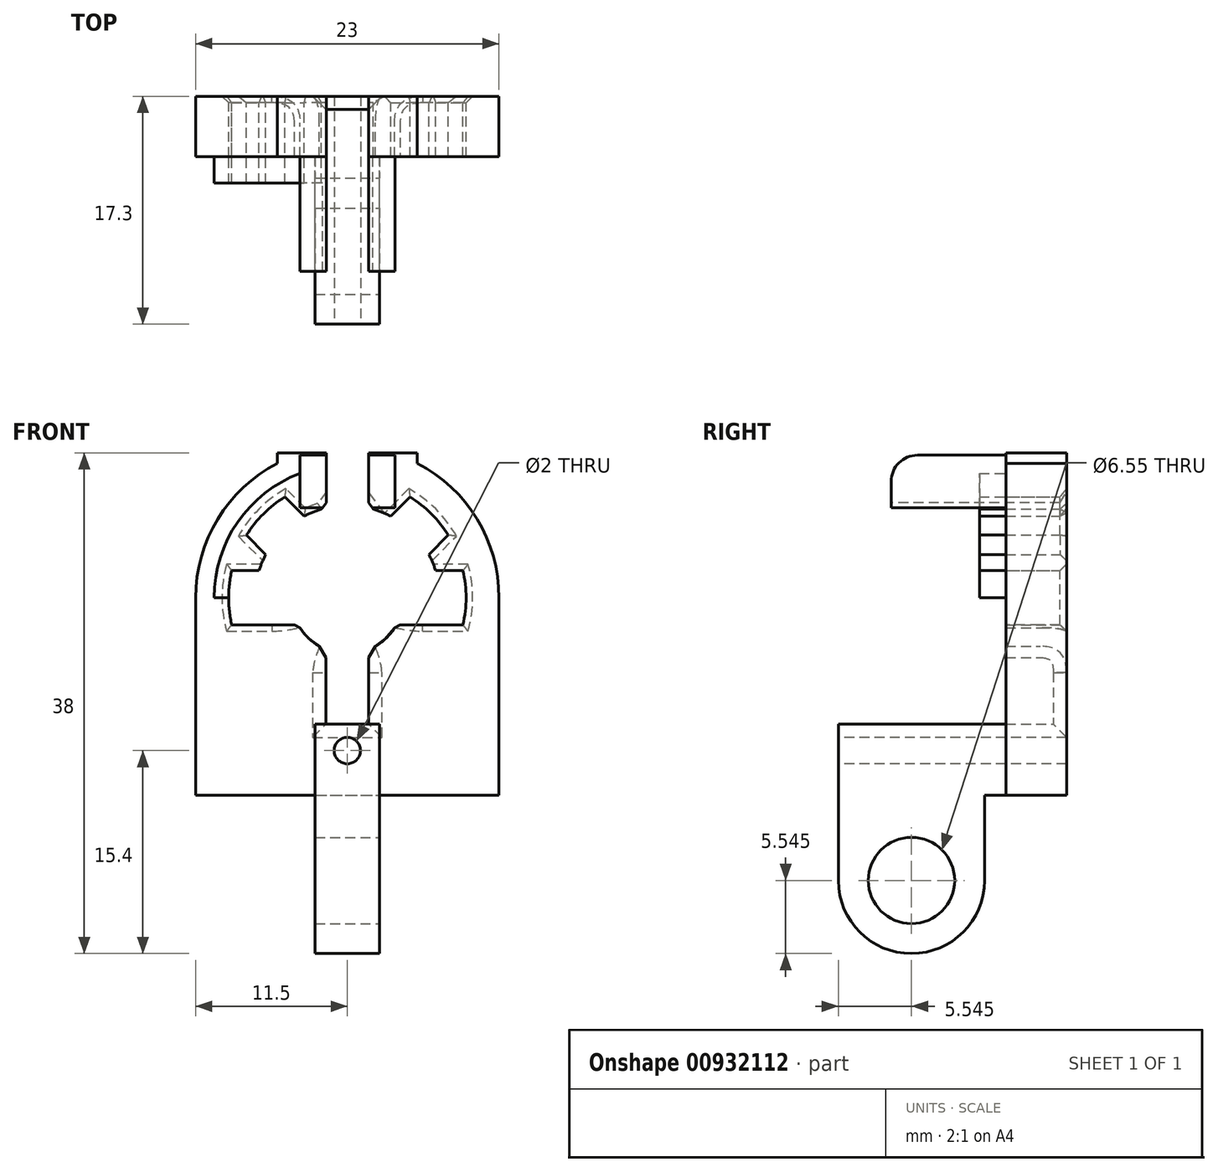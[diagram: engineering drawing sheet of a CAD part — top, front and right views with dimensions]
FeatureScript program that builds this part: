
annotation { "Feature Type Name" : "Feature", "Feature Type Description" : "" }
export const myFeature = defineFeature(function(context is Context, id is Id, definition is map)
    precondition{}
    {
        {
            var Q0;
            Q0=qCreatedBy(makeId("Front.planeOp"),FACE);
            var sketch = newSketch(context, id + "F0", { "sketchPlane" : qUnion([Q0])});
            skLineSegment(sketch, "E0", {"start": v(0, 0) * mm, "end": v(0, 30) * mm, "construction": true});
            skLineSegment(sketch, "E1.top", {"start": v(-11.5, 0) * mm, "end": v(11.5, 0) * mm});
            skPoint(sketch, "E1.middle", {"position": v(0, 15) * mm});
            skLineSegment(sketch, "E2", {"start": v(-11.5, 0) * mm, "end": v(-11.5, 15) * mm});
            skLineSegment(sketch, "E3", {"start": v(11.5, 0) * mm, "end": v(11.5, 15) * mm});
            skArc(sketch, "E4", {"start": v(11.5, 15) * mm, "mid": v(9.83, 20.97) * mm, "end": v(5.3, 25.2) * mm});
            skLineSegment(sketch, "E5.top", {"start": v(-5.3, 26) * mm, "end": v(-1.6, 26) * mm});
            skLineSegment(sketch, "E5.left", {"start": v(-5.3, 25.2) * mm, "end": v(-5.3, 26) * mm});
            skLineSegment(sketch, "E5.right", {"start": v(5.3, 25.2) * mm, "end": v(5.3, 26) * mm});
            skArc(sketch, "E6.trimOffspring", {"start": v(-5.3, 25.2) * mm, "mid": v(-9.83, 20.97) * mm, "end": v(-11.5, 15) * mm});
            skLineSegment(sketch, "E7.left", {"start": v(-1.6, 26) * mm, "end": v(-1.6, 21.81) * mm});
            skLineSegment(sketch, "E7.right", {"start": v(1.6, 26) * mm, "end": v(1.6, 21.81) * mm});
            skPoint(sketch, "E7.middle", {"position": v(0, 23.9) * mm});
            skArc(sketch, "E8", {"start": v(6.7, 17.05) * mm, "mid": v(6.47, 17.68) * mm, "end": v(6.18, 18.28) * mm});
            skLineSegment(sketch, "E9", {"start": v(8.76, 17.05) * mm, "end": v(6.7, 17.05) * mm});
            skLineSegment(sketch, "E10", {"start": v(8.76, 12.95) * mm, "end": v(6.7, 12.95) * mm});
            skLineSegment(sketch, "E11", {"start": v(1.6, 26) * mm, "end": v(5.3, 26) * mm});
            skLineSegment(sketch, "E12.1.0", {"start": v(4.75, 22.65) * mm, "end": v(3.28, 21.18) * mm});
            skLineSegment(sketch, "E12.1.1", {"start": v(7.65, 19.75) * mm, "end": v(6.18, 18.28) * mm});
            skLineSegment(sketch, "E12.3.0", {"start": v(-7.65, 19.75) * mm, "end": v(-6.18, 18.28) * mm});
            skLineSegment(sketch, "E12.3.1", {"start": v(-4.75, 22.65) * mm, "end": v(-3.28, 21.18) * mm});
            skLineSegment(sketch, "E12.4.0", {"start": v(-8.76, 12.95) * mm, "end": v(-6.7, 12.95) * mm});
            skLineSegment(sketch, "E12.4.1", {"start": v(-8.76, 17.05) * mm, "end": v(-6.7, 17.05) * mm});
            skArc(sketch, "E13.trimOffspring", {"start": v(-6.18, 18.28) * mm, "mid": v(-6.47, 17.68) * mm, "end": v(-6.7, 17.05) * mm});
            skArc(sketch, "E14.trimOffspring", {"start": v(-1.6, 21.81) * mm, "mid": v(-2.46, 21.55) * mm, "end": v(-3.28, 21.18) * mm});
            skArc(sketch, "E15.trimOffspring", {"start": v(3.28, 21.18) * mm, "mid": v(2.46, 21.55) * mm, "end": v(1.6, 21.81) * mm});
            skArc(sketch, "E16.trimOffspring", {"start": v(-8.76, 17.05) * mm, "mid": v(-9, 15) * mm, "end": v(-8.76, 12.95) * mm});
            skArc(sketch, "E17.trimOffspring", {"start": v(-4.75, 22.65) * mm, "mid": v(-6.36, 21.36) * mm, "end": v(-7.65, 19.75) * mm});
            skArc(sketch, "E18.trimOffspring", {"start": v(7.65, 19.75) * mm, "mid": v(6.36, 21.36) * mm, "end": v(4.75, 22.65) * mm});
            skArc(sketch, "E19.trimOffspring", {"start": v(8.76, 12.95) * mm, "mid": v(9, 15) * mm, "end": v(8.76, 17.05) * mm});
            skArc(sketch, "E20", {"start": v(-3.72, 12.95) * mm, "mid": v(-2.83, 11.83) * mm, "end": v(-1.62, 11.07) * mm});
            skLineSegment(sketch, "E21", {"start": v(-6.7, 12.95) * mm, "end": v(-3.72, 12.95) * mm});
            skLineSegment(sketch, "E22", {"start": v(6.7, 12.95) * mm, "end": v(3.72, 12.95) * mm});
            skLineSegment(sketch, "E23.top", {"start": v(-1.63, 5.4) * mm, "end": v(1.62, 5.4) * mm});
            skLineSegment(sketch, "E23.left", {"start": v(-1.63, 11.07) * mm, "end": v(-1.63, 5.4) * mm});
            skLineSegment(sketch, "E23.right", {"start": v(1.62, 11.07) * mm, "end": v(1.62, 5.4) * mm});
            skPoint(sketch, "E23.middle", {"position": v(0, 8.85) * mm});
            skArc(sketch, "E24.trimOffspring", {"start": v(1.62, 11.07) * mm, "mid": v(2.83, 11.83) * mm, "end": v(3.72, 12.95) * mm});
            skSolve(sketch);
        }
        {
            var Q0;
            Q0 = qSketchRegion(id + "F0", true);
            extrude(context, id + "F1", {"entities" : qUnion([Q0]), "depth" : 4.6 * mm, "offsetDistance" : 25 * mm});
        }
        {
            var Q0;
            Q0=makeQuery(id+"F1.opExtrude","CAP_FACE",FACE,{"disambiguationData":[OSD([sQuery(id+"F0.wireOp",EDGE,"E1.top"),sQuery(id+"F0.wireOp",EDGE,"E2"),sQuery(id+"F0.wireOp",EDGE,"E3"),sQuery(id+"F0.wireOp",EDGE,"E4"),sQuery(id+"F0.wireOp",EDGE,"E5.top"),sQuery(id+"F0.wireOp",EDGE,"E5.left"),sQuery(id+"F0.wireOp",EDGE,"E5.right"),sQuery(id+"F0.wireOp",EDGE,"E6.trimOffspring"),sQuery(id+"F0.wireOp",EDGE,"E7.left"),sQuery(id+"F0.wireOp",EDGE,"E7.right"),sQuery(id+"F0.wireOp",EDGE,"E8"),sQuery(id+"F0.wireOp",EDGE,"E9"),sQuery(id+"F0.wireOp",EDGE,"E10"),sQuery(id+"F0.wireOp",EDGE,"E11"),sQuery(id+"F0.wireOp",EDGE,"E12.1.0"),sQuery(id+"F0.wireOp",EDGE,"E12.1.1"),sQuery(id+"F0.wireOp",EDGE,"E12.3.0"),sQuery(id+"F0.wireOp",EDGE,"E12.3.1"),sQuery(id+"F0.wireOp",EDGE,"E12.4.0"),sQuery(id+"F0.wireOp",EDGE,"E12.4.1"),sQuery(id+"F0.wireOp",EDGE,"E13.trimOffspring"),sQuery(id+"F0.wireOp",EDGE,"E14.trimOffspring"),sQuery(id+"F0.wireOp",EDGE,"E15.trimOffspring"),sQuery(id+"F0.wireOp",EDGE,"E16.trimOffspring"),sQuery(id+"F0.wireOp",EDGE,"E17.trimOffspring"),sQuery(id+"F0.wireOp",EDGE,"E18.trimOffspring"),sQuery(id+"F0.wireOp",EDGE,"E19.trimOffspring"),sQuery(id+"F0.wireOp",EDGE,"E20"),sQuery(id+"F0.wireOp",EDGE,"E21"),sQuery(id+"F0.wireOp",EDGE,"E22"),sQuery(id+"F0.wireOp",EDGE,"E23.top"),sQuery(id+"F0.wireOp",EDGE,"E23.left"),sQuery(id+"F0.wireOp",EDGE,"E23.right"),sQuery(id+"F0.wireOp",EDGE,"E24.trimOffspring")])],"isStart":false});
            var sketch = newSketch(context, id + "F2", { "sketchPlane" : qUnion([Q0])});
            skLineSegment(sketch, "E25.bottom", {"start": v(-2.45, 5.4) * mm, "end": v(2.45, 5.4) * mm});
            skLineSegment(sketch, "E25.top", {"start": v(-2.45, -12) * mm, "end": v(2.45, -12) * mm});
            skLineSegment(sketch, "E25.left", {"start": v(-2.45, 5.4) * mm, "end": v(-2.45, -12) * mm});
            skLineSegment(sketch, "E25.right", {"start": v(2.45, 5.4) * mm, "end": v(2.45, -12) * mm});
            skPoint(sketch, "E25.middle", {"position": v(0, -3.3) * mm});
            skSolve(sketch);
        }
        {
            var Q0;
            Q0 = qSketchRegion(id + "F2", true);
            extrude(context, id + "F3", {"entities" : qUnion([Q0]), "operationType" : NewBodyOperationType.ADD, "depth" : 12.7 * mm, "offsetDistance" : 25 * mm});
        }
        {
            var Q0;
            Q0=makeQuery(id+"F3.opExtrude","SWEPT_FACE",FACE,{"disambiguationData":[OSD([sQuery(id+"F2.wireOp",EDGE,"E25.right")])]});
            var sketch = newSketch(context, id + "F4", { "sketchPlane" : qUnion([Q0])});
            skLineSegment(sketch, "E26.bottom", {"start": v(-4.6, 0) * mm, "end": v(-6.21, 0) * mm});
            skLineSegment(sketch, "E26.top", {"start": v(-4.6, -12) * mm, "end": v(-6.2, -12) * mm});
            skLineSegment(sketch, "E26.left", {"start": v(-4.6, 0) * mm, "end": v(-4.6, -12) * mm});
            skLineSegment(sketch, "E26.right", {"start": v(-6.21, 0) * mm, "end": v(-6.2, -12) * mm});
            skSolve(sketch);
        }
        {
            var Q0;
            Q0 = qSketchRegion(id + "F4", true);
            extrude(context, id + "F5", {"entities" : qUnion([Q0]), "operationType" : NewBodyOperationType.REMOVE, "oppositeDirection" : true, "depth" : 25 * mm, "offsetDistance" : 25 * mm});
        }
        {
            var Q0;
            Q0=makeQuery(id+"F3.opExtrude","SWEPT_FACE",FACE,{"disambiguationData":[OSD([sQuery(id+"F2.wireOp",EDGE,"E25.right")])]});
            var sketch = newSketch(context, id + "F6", { "sketchPlane" : qUnion([Q0])});
            skArc(sketch, "E27", {"start": v(-17.3, -6.45) * mm, "mid": v(-11.75, -12) * mm, "end": v(-6.2, -6.45) * mm});
            skPoint(sketch, "E27.centerSnap0", {"position": v(-11.75, -12) * mm});
            skLineSegment(sketch, "E28", {"start": v(-17.3, -6.45) * mm, "end": v(-17.3, -14.94) * mm});
            skLineSegment(sketch, "E29", {"start": v(-17.3, -14.94) * mm, "end": v(-6.2, -14.94) * mm});
            skLineSegment(sketch, "E30", {"start": v(-6.2, -14.94) * mm, "end": v(-6.2, -6.45) * mm});
            skCircle(sketch, "E31", {"center": v(-11.75, -6.45) * mm, "radius": 3.28 * mm});
            skSolve(sketch);
        }
        {
            var Q0;
            Q0 = qSketchRegion(id + "F6", true);
            extrude(context, id + "F7", {"entities" : qUnion([Q0]), "operationType" : NewBodyOperationType.REMOVE, "oppositeDirection" : true, "depth" : 25 * mm, "offsetDistance" : 25 * mm});
        }
        {
            var Q0;
            Q0=makeQuery(id+"F3.opExtrude","CAP_FACE",FACE,{"disambiguationData":[OSD([sQuery(id+"F2.wireOp",EDGE,"E25.bottom"),sQuery(id+"F2.wireOp",EDGE,"E25.top"),sQuery(id+"F2.wireOp",EDGE,"E25.left"),sQuery(id+"F2.wireOp",EDGE,"E25.right")])],"isStart":false});
            var sketch = newSketch(context, id + "F8", { "sketchPlane" : qUnion([Q0])});
            skCircle(sketch, "E32", {"center": v(0, 3.4) * mm, "radius": 1 * mm});
            skPoint(sketch, "E32.centerSnap0", {"position": v(0, 5.4) * mm});
            skSolve(sketch);
        }
        {
            var Q0;
            Q0 = qSketchRegion(id + "F8", true);
            extrude(context, id + "F9", {"entities" : qUnion([Q0]), "operationType" : NewBodyOperationType.REMOVE, "endBound" : BoundingType.THROUGH_ALL, "oppositeDirection" : true, "depth" : 25 * mm, "offsetDistance" : 25 * mm});
        }
        {
            var Q0;
            {var subQ0=sQuery(id+"F0.wireOp",EDGE,"E12.3.1");var subQ1=sQuery(id+"F0.wireOp",EDGE,"E24.trimOffspring");var subQ2=sQuery(id+"F0.wireOp",EDGE,"E23.right");var subQ3=sQuery(id+"F0.wireOp",EDGE,"E23.left");var subQ4=sQuery(id+"F0.wireOp",EDGE,"E23.top");var subQ5=sQuery(id+"F0.wireOp",EDGE,"E22");var subQ6=sQuery(id+"F0.wireOp",EDGE,"E21");var subQ7=sQuery(id+"F0.wireOp",EDGE,"E20");var subQ8=sQuery(id+"F0.wireOp",EDGE,"E19.trimOffspring");var subQ9=sQuery(id+"F0.wireOp",EDGE,"E18.trimOffspring");var subQ10=sQuery(id+"F0.wireOp",EDGE,"E17.trimOffspring");var subQ11=sQuery(id+"F0.wireOp",EDGE,"E16.trimOffspring");var subQ12=sQuery(id+"F0.wireOp",EDGE,"E15.trimOffspring");var subQ13=sQuery(id+"F0.wireOp",EDGE,"E14.trimOffspring");var subQ14=sQuery(id+"F0.wireOp",EDGE,"E13.trimOffspring");var subQ15=sQuery(id+"F0.wireOp",EDGE,"E12.4.1");var subQ16=sQuery(id+"F0.wireOp",EDGE,"E12.4.0");var subQ17=sQuery(id+"F0.wireOp",EDGE,"E12.3.0");var subQ18=sQuery(id+"F0.wireOp",EDGE,"E12.1.1");var subQ19=sQuery(id+"F0.wireOp",EDGE,"E12.1.0");var subQ20=sQuery(id+"F0.wireOp",EDGE,"E11");var subQ21=sQuery(id+"F0.wireOp",EDGE,"E10");var subQ22=sQuery(id+"F0.wireOp",EDGE,"E9");var subQ23=sQuery(id+"F0.wireOp",EDGE,"E8");var subQ24=sQuery(id+"F0.wireOp",EDGE,"E7.right");var subQ25=sQuery(id+"F0.wireOp",EDGE,"E7.left");var subQ26=sQuery(id+"F0.wireOp",EDGE,"E6.trimOffspring");var subQ27=sQuery(id+"F0.wireOp",EDGE,"E5.right");var subQ28=sQuery(id+"F0.wireOp",EDGE,"E5.left");var subQ29=sQuery(id+"F0.wireOp",EDGE,"E5.top");var subQ30=sQuery(id+"F0.wireOp",EDGE,"E4");var subQ31=sQuery(id+"F0.wireOp",EDGE,"E3");var subQ32=sQuery(id+"F0.wireOp",EDGE,"E2");var subQ33=sQuery(id+"F0.wireOp",EDGE,"E1.top");var subQ34=makeQuery(id+"F1.opExtrude","CAP_FACE",FACE,{"disambiguationData":[OSD([subQ33,subQ32,subQ31,subQ30,subQ29,subQ28,subQ27,subQ26,subQ25,subQ24,subQ23,subQ22,subQ21,subQ20,subQ19,subQ18,subQ17,subQ0,subQ16,subQ15,subQ14,subQ13,subQ12,subQ11,subQ10,subQ9,subQ8,subQ7,subQ6,subQ5,subQ4,subQ3,subQ2,subQ1])],"isStart":false});Q0=makeQuery(id+"F3.boolean.opBoolean","SPLIT",FACE,{"disambiguationData":[TD([makeQuery(id+"F1.opExtrude","SWEPT_FACE",FACE,{"disambiguationData":[OSD([subQ32])]})])],"derivedFrom":subQ34});}
            var sketch = newSketch(context, id + "F10", { "sketchPlane" : qUnion([Q0])});
            skLineSegment(sketch, "E33", {"start": v(-9, 15) * mm, "end": v(-10.1, 15) * mm});
            skArc(sketch, "E34", {"start": v(-1.6, 24.97) * mm, "mid": v(-7.69, 21.55) * mm, "end": v(-10.1, 15) * mm});
            skLineSegment(sketch, "E35", {"start": v(-1.6, 24.97) * mm, "end": v(-1.6, 21.81) * mm});
            skArc(sketch, "E36.0", {"start": v(-1.6, 21.81) * mm, "mid": v(-2.46, 21.55) * mm, "end": v(-3.28, 21.18) * mm});
            skArc(sketch, "E36.1", {"start": v(-6.18, 18.28) * mm, "mid": v(-6.47, 17.68) * mm, "end": v(-6.7, 17.05) * mm});
            skArc(sketch, "E36.2", {"start": v(-8.76, 17.05) * mm, "mid": v(-8.94, 16.03) * mm, "end": v(-9, 15) * mm});
            skLineSegment(sketch, "E37", {"start": v(-7.65, 19.75) * mm, "end": v(-6.18, 18.28) * mm});
            skArc(sketch, "E38.0", {"start": v(-4.75, 22.65) * mm, "mid": v(-6.36, 21.36) * mm, "end": v(-7.65, 19.75) * mm});
            skLineSegment(sketch, "E39", {"start": v(-4.75, 22.65) * mm, "end": v(-3.28, 21.18) * mm});
            skLineSegment(sketch, "E40", {"start": v(-8.76, 17.05) * mm, "end": v(-6.7, 17.05) * mm});
            skPoint(sketch, "E41.orphan", {"position": v(-8.76, 12.95) * mm});
            skSolve(sketch);
        }
        {
            var Q0;
            Q0=makeQuery(id+"F10.imprint","IMPRINT",FACE,{"disambiguationData":[TD([[makeQuery(id+"F10.imprint","IMPRINT",EDGE,{"derivedFrom":sQuery(id+"F10.wireOp",EDGE,"E33")}),-1.0]])]});
            extrude(context, id + "F11", {"entities" : qUnion([Q0]), "operationType" : NewBodyOperationType.ADD, "depth" : 2 * mm, "offsetDistance" : 25 * mm});
        }
        {
            var Q0;
            {var subQ0=sQuery(id+"F0.wireOp",EDGE,"E12.1.1");var subQ2=sQuery(id+"F0.wireOp",EDGE,"E22");var subQ3=sQuery(id+"F0.wireOp",EDGE,"E10");var subQ4=sQuery(id+"F0.wireOp",EDGE,"E9");var subQ5=sQuery(id+"F0.wireOp",EDGE,"E8");var subQ6=sQuery(id+"F0.wireOp",EDGE,"E7.right");var subQ8=sQuery(id+"F0.wireOp",EDGE,"E1.top");var subQ9=sQuery(id+"F0.wireOp",EDGE,"E12.1.0");var subQ10=sQuery(id+"F0.wireOp",EDGE,"E4");var subQ11=sQuery(id+"F0.wireOp",EDGE,"E19.trimOffspring");var subQ12=sQuery(id+"F0.wireOp",EDGE,"E3");var subQ13=sQuery(id+"F0.wireOp",EDGE,"E18.trimOffspring");var subQ14=sQuery(id+"F0.wireOp",EDGE,"E5.right");var subQ16=sQuery(id+"F0.wireOp",EDGE,"E15.trimOffspring");var subQ17=sQuery(id+"F0.wireOp",EDGE,"E23.top");var subQ18=sQuery(id+"F0.wireOp",EDGE,"E23.right");var subQ19=sQuery(id+"F0.wireOp",EDGE,"E24.trimOffspring");var subQ20=sQuery(id+"F0.wireOp",EDGE,"E23.left");var subQ21=sQuery(id+"F0.wireOp",EDGE,"E21");var subQ22=sQuery(id+"F0.wireOp",EDGE,"E20");var subQ23=sQuery(id+"F0.wireOp",EDGE,"E17.trimOffspring");var subQ24=sQuery(id+"F0.wireOp",EDGE,"E16.trimOffspring");var subQ25=sQuery(id+"F0.wireOp",EDGE,"E14.trimOffspring");var subQ26=sQuery(id+"F0.wireOp",EDGE,"E13.trimOffspring");var subQ27=sQuery(id+"F0.wireOp",EDGE,"E12.4.1");var subQ28=sQuery(id+"F0.wireOp",EDGE,"E12.4.0");var subQ29=sQuery(id+"F0.wireOp",EDGE,"E12.3.1");var subQ30=sQuery(id+"F0.wireOp",EDGE,"E12.3.0");var subQ31=sQuery(id+"F0.wireOp",EDGE,"E11");var subQ32=sQuery(id+"F0.wireOp",EDGE,"E7.left");var subQ33=sQuery(id+"F0.wireOp",EDGE,"E6.trimOffspring");var subQ34=sQuery(id+"F0.wireOp",EDGE,"E5.left");var subQ35=sQuery(id+"F0.wireOp",EDGE,"E5.top");var subQ36=sQuery(id+"F0.wireOp",EDGE,"E2");var subQ37=makeQuery(id+"F1.opExtrude","CAP_FACE",FACE,{"disambiguationData":[OSD([subQ8,subQ36,subQ12,subQ10,subQ35,subQ34,subQ14,subQ33,subQ32,subQ6,subQ5,subQ4,subQ3,subQ31,subQ9,subQ0,subQ30,subQ29,subQ28,subQ27,subQ26,subQ25,subQ16,subQ24,subQ23,subQ13,subQ11,subQ22,subQ21,subQ2,subQ17,subQ20,subQ18,subQ19])],"isStart":false});Q0=makeQuery(id+"F3.boolean.opBoolean","SPLIT",FACE,{"disambiguationData":[TD([makeQuery(id+"F1.opExtrude","SWEPT_FACE",FACE,{"disambiguationData":[OSD([subQ12])]})])],"derivedFrom":subQ37});}
            var sketch = newSketch(context, id + "F12", { "sketchPlane" : qUnion([Q0])});
            skLineSegment(sketch, "E42", {"start": v(1.6, 25.81) * mm, "end": v(3.6, 25.81) * mm});
            skLineSegment(sketch, "E43", {"start": v(3.6, 25.81) * mm, "end": v(3.6, 21.81) * mm});
            skLineSegment(sketch, "E44", {"start": v(3.6, 21.81) * mm, "end": v(1.6, 21.81) * mm});
            skLineSegment(sketch, "E45", {"start": v(0, 15) * mm, "end": v(0, 29.93) * mm, "construction": true});
            skLineSegment(sketch, "E46", {"start": v(1.6, 25.81) * mm, "end": v(1.6, 21.81) * mm});
            skLineSegment(sketch, "E47.MirrorCS", {"start": v(-3.6, 21.81) * mm, "end": v(-1.6, 21.81) * mm});
            skLineSegment(sketch, "E48.MirrorCS", {"start": v(-1.6, 25.81) * mm, "end": v(-1.6, 21.81) * mm});
            skLineSegment(sketch, "E49.MirrorCS", {"start": v(-3.6, 25.81) * mm, "end": v(-3.6, 21.81) * mm});
            skLineSegment(sketch, "E50.MirrorCS", {"start": v(-1.6, 25.81) * mm, "end": v(-3.6, 25.81) * mm});
            skSolve(sketch);
        }
        {
            var Q0;
            Q0 = qSketchRegion(id + "F12", true);
            extrude(context, id + "F13", {"entities" : qUnion([Q0]), "operationType" : NewBodyOperationType.ADD, "depth" : 8.7 * mm, "offsetDistance" : 25 * mm});
        }
        {
            var Q0;
            Q0=makeQuery(id+"F13.opExtrude","CAP_EDGE",EDGE,{"disambiguationData":[OSD([sQuery(id+"F12.wireOp",EDGE,"E42")])],"isStart":false});
            var Q1;
            Q1=makeQuery(id+"F13.opExtrude","CAP_EDGE",EDGE,{"disambiguationData":[OSD([sQuery(id+"F12.wireOp",EDGE,"E50.MirrorCS")])],"isStart":false});
            fillet(context, id + "F14", {"entities" : qUnion([Q0, Q1]), "radius" : 2 * mm, "tangentPropagation" : true, "allowEdgeOverflow" : false});
        }
        {
            var Q0;
            Q0=makeQuery(id+"F1.opExtrude","CAP_EDGE",EDGE,{"disambiguationData":[OSD([sQuery(id+"F0.wireOp",EDGE,"E24.trimOffspring")])],"isStart":true});
            var Q1;
            Q1=makeQuery(id+"F1.opExtrude","CAP_EDGE",EDGE,{"disambiguationData":[OSD([sQuery(id+"F0.wireOp",EDGE,"E20")])],"isStart":true});
            fillet(context, id + "F15", {"entities" : qUnion([Q0, Q1]), "radius" : 2 * mm, "tangentPropagation" : true, "rho" : 0.5, "crossSection" : FilletCrossSection.CONIC, "allowEdgeOverflow" : false});
        }
        {
            var Q0;
            Q0=makeQuery(id+"F1.opExtrude","CAP_EDGE",EDGE,{"disambiguationData":[OSD([sQuery(id+"F0.wireOp",EDGE,"E23.right")])],"isStart":true});
            var Q1;
            Q1=makeQuery(id+"F1.opExtrude","CAP_EDGE",EDGE,{"disambiguationData":[OSD([sQuery(id+"F0.wireOp",EDGE,"E23.left")])],"isStart":true});
            var Q2;
            Q2=makeQuery(id+"F1.opExtrude","CAP_EDGE",EDGE,{"disambiguationData":[OSD([sQuery(id+"F0.wireOp",EDGE,"E23.top")])],"isStart":true});
            chamfer(context, id + "F16", {"entities" : qUnion([Q0, Q1, Q2]), "width" : 1 * mm, "tangentPropagation" : true});
        }
        {
            var Q0;
            Q0=makeQuery(id+"F11.boolean.opBoolean","MERGE",EDGE,{"derivedFrom":[makeQuery(id+"F1.opExtrude","SWEPT_EDGE",EDGE,{"disambiguationData":[OSD([sQuery(id+"F0.wireOp",EDGE,"E7.left"),sQuery(id+"F0.wireOp",EDGE,"E14.trimOffspring")])]}),makeQuery(id+"F11.opExtrude","SWEPT_EDGE",EDGE,{"disambiguationData":[OSD([sQuery(id+"F10.wireOp",EDGE,"E35"),sQuery(id+"F10.wireOp",EDGE,"E36.0")])]})]});
            var Q1;
            Q1=makeQuery(id+"F1.opExtrude","SWEPT_EDGE",EDGE,{"disambiguationData":[OSD([sQuery(id+"F0.wireOp",EDGE,"E7.right"),sQuery(id+"F0.wireOp",EDGE,"E15.trimOffspring")])]});
            chamfer(context, id + "F17", {"entities" : qUnion([Q0, Q1]), "width" : 0.5 * mm, "tangentPropagation" : true});
        }
        {
            var Q0;
            Q0=makeQuery(id+"F1.opExtrude","CAP_EDGE",EDGE,{"disambiguationData":[OSD([sQuery(id+"F0.wireOp",EDGE,"E19.trimOffspring")])],"isStart":true});
            var Q1;
            Q1=makeQuery(id+"F1.opExtrude","CAP_EDGE",EDGE,{"disambiguationData":[OSD([sQuery(id+"F0.wireOp",EDGE,"E9")])],"isStart":true});
            var Q2;
            Q2=makeQuery(id+"F1.opExtrude","CAP_EDGE",EDGE,{"disambiguationData":[OSD([sQuery(id+"F0.wireOp",EDGE,"E12.1.1")])],"isStart":true});
            var Q3;
            Q3=makeQuery(id+"F1.opExtrude","CAP_EDGE",EDGE,{"disambiguationData":[OSD([sQuery(id+"F0.wireOp",EDGE,"E18.trimOffspring")])],"isStart":true});
            var Q4;
            Q4=makeQuery(id+"F1.opExtrude","CAP_EDGE",EDGE,{"disambiguationData":[OSD([sQuery(id+"F0.wireOp",EDGE,"E12.1.0")])],"isStart":true});
            var Q5;
            {var subQ0=sQuery(id+"F0.wireOp",EDGE,"E15.trimOffspring");var subQ1=sQuery(id+"F0.wireOp",EDGE,"E7.right");Q5=makeQuery(id+"F17.opChamfer","BLEND_EDGE",EDGE,{"blendedFrom":[makeQuery(id+"F1.opExtrude","SWEPT_EDGE",EDGE,{"disambiguationData":[OSD([subQ1,subQ0])]}),makeQuery(id+"F1.opExtrude","CAP_FACE",FACE,{"disambiguationData":[OSD([sQuery(id+"F0.wireOp",EDGE,"E1.top"),sQuery(id+"F0.wireOp",EDGE,"E2"),sQuery(id+"F0.wireOp",EDGE,"E3"),sQuery(id+"F0.wireOp",EDGE,"E4"),sQuery(id+"F0.wireOp",EDGE,"E5.top"),sQuery(id+"F0.wireOp",EDGE,"E5.left"),sQuery(id+"F0.wireOp",EDGE,"E5.right"),sQuery(id+"F0.wireOp",EDGE,"E6.trimOffspring"),sQuery(id+"F0.wireOp",EDGE,"E7.left"),subQ1,sQuery(id+"F0.wireOp",EDGE,"E8"),sQuery(id+"F0.wireOp",EDGE,"E9"),sQuery(id+"F0.wireOp",EDGE,"E10"),sQuery(id+"F0.wireOp",EDGE,"E11"),sQuery(id+"F0.wireOp",EDGE,"E12.1.0"),sQuery(id+"F0.wireOp",EDGE,"E12.1.1"),sQuery(id+"F0.wireOp",EDGE,"E12.3.0"),sQuery(id+"F0.wireOp",EDGE,"E12.3.1"),sQuery(id+"F0.wireOp",EDGE,"E12.4.0"),sQuery(id+"F0.wireOp",EDGE,"E12.4.1"),sQuery(id+"F0.wireOp",EDGE,"E13.trimOffspring"),sQuery(id+"F0.wireOp",EDGE,"E14.trimOffspring"),subQ0,sQuery(id+"F0.wireOp",EDGE,"E16.trimOffspring"),sQuery(id+"F0.wireOp",EDGE,"E17.trimOffspring"),sQuery(id+"F0.wireOp",EDGE,"E18.trimOffspring"),sQuery(id+"F0.wireOp",EDGE,"E19.trimOffspring"),sQuery(id+"F0.wireOp",EDGE,"E20"),sQuery(id+"F0.wireOp",EDGE,"E21"),sQuery(id+"F0.wireOp",EDGE,"E22"),sQuery(id+"F0.wireOp",EDGE,"E23.top"),sQuery(id+"F0.wireOp",EDGE,"E23.left"),sQuery(id+"F0.wireOp",EDGE,"E23.right"),sQuery(id+"F0.wireOp",EDGE,"E24.trimOffspring")])],"isStart":true})],"blendedInto":[makeQuery(id+"F1.opExtrude","CAP_FACE",FACE,{"disambiguationData":[OSD([sQuery(id+"F0.wireOp",EDGE,"E1.top"),sQuery(id+"F0.wireOp",EDGE,"E2"),sQuery(id+"F0.wireOp",EDGE,"E3"),sQuery(id+"F0.wireOp",EDGE,"E4"),sQuery(id+"F0.wireOp",EDGE,"E5.top"),sQuery(id+"F0.wireOp",EDGE,"E5.left"),sQuery(id+"F0.wireOp",EDGE,"E5.right"),sQuery(id+"F0.wireOp",EDGE,"E6.trimOffspring"),sQuery(id+"F0.wireOp",EDGE,"E7.left"),subQ1,sQuery(id+"F0.wireOp",EDGE,"E8"),sQuery(id+"F0.wireOp",EDGE,"E9"),sQuery(id+"F0.wireOp",EDGE,"E10"),sQuery(id+"F0.wireOp",EDGE,"E11"),sQuery(id+"F0.wireOp",EDGE,"E12.1.0"),sQuery(id+"F0.wireOp",EDGE,"E12.1.1"),sQuery(id+"F0.wireOp",EDGE,"E12.3.0"),sQuery(id+"F0.wireOp",EDGE,"E12.3.1"),sQuery(id+"F0.wireOp",EDGE,"E12.4.0"),sQuery(id+"F0.wireOp",EDGE,"E12.4.1"),sQuery(id+"F0.wireOp",EDGE,"E13.trimOffspring"),sQuery(id+"F0.wireOp",EDGE,"E14.trimOffspring"),subQ0,sQuery(id+"F0.wireOp",EDGE,"E16.trimOffspring"),sQuery(id+"F0.wireOp",EDGE,"E17.trimOffspring"),sQuery(id+"F0.wireOp",EDGE,"E18.trimOffspring"),sQuery(id+"F0.wireOp",EDGE,"E19.trimOffspring"),sQuery(id+"F0.wireOp",EDGE,"E20"),sQuery(id+"F0.wireOp",EDGE,"E21"),sQuery(id+"F0.wireOp",EDGE,"E22"),sQuery(id+"F0.wireOp",EDGE,"E23.top"),sQuery(id+"F0.wireOp",EDGE,"E23.left"),sQuery(id+"F0.wireOp",EDGE,"E23.right"),sQuery(id+"F0.wireOp",EDGE,"E24.trimOffspring")])],"isStart":true})]});}
            var Q6;
            {var subQ0=sQuery(id+"F0.wireOp",EDGE,"E14.trimOffspring");var subQ1=sQuery(id+"F0.wireOp",EDGE,"E7.left");Q6=makeQuery(id+"F17.opChamfer","BLEND_EDGE",EDGE,{"blendedFrom":[makeQuery(id+"F11.boolean.opBoolean","MERGE",EDGE,{"derivedFrom":[makeQuery(id+"F1.opExtrude","SWEPT_EDGE",EDGE,{"disambiguationData":[OSD([subQ1,subQ0])]}),makeQuery(id+"F11.opExtrude","SWEPT_EDGE",EDGE,{"disambiguationData":[OSD([sQuery(id+"F10.wireOp",EDGE,"E35"),sQuery(id+"F10.wireOp",EDGE,"E36.0")])]})]}),makeQuery(id+"F1.opExtrude","CAP_FACE",FACE,{"disambiguationData":[OSD([sQuery(id+"F0.wireOp",EDGE,"E1.top"),sQuery(id+"F0.wireOp",EDGE,"E2"),sQuery(id+"F0.wireOp",EDGE,"E3"),sQuery(id+"F0.wireOp",EDGE,"E4"),sQuery(id+"F0.wireOp",EDGE,"E5.top"),sQuery(id+"F0.wireOp",EDGE,"E5.left"),sQuery(id+"F0.wireOp",EDGE,"E5.right"),sQuery(id+"F0.wireOp",EDGE,"E6.trimOffspring"),subQ1,sQuery(id+"F0.wireOp",EDGE,"E7.right"),sQuery(id+"F0.wireOp",EDGE,"E8"),sQuery(id+"F0.wireOp",EDGE,"E9"),sQuery(id+"F0.wireOp",EDGE,"E10"),sQuery(id+"F0.wireOp",EDGE,"E11"),sQuery(id+"F0.wireOp",EDGE,"E12.1.0"),sQuery(id+"F0.wireOp",EDGE,"E12.1.1"),sQuery(id+"F0.wireOp",EDGE,"E12.3.0"),sQuery(id+"F0.wireOp",EDGE,"E12.3.1"),sQuery(id+"F0.wireOp",EDGE,"E12.4.0"),sQuery(id+"F0.wireOp",EDGE,"E12.4.1"),sQuery(id+"F0.wireOp",EDGE,"E13.trimOffspring"),subQ0,sQuery(id+"F0.wireOp",EDGE,"E15.trimOffspring"),sQuery(id+"F0.wireOp",EDGE,"E16.trimOffspring"),sQuery(id+"F0.wireOp",EDGE,"E17.trimOffspring"),sQuery(id+"F0.wireOp",EDGE,"E18.trimOffspring"),sQuery(id+"F0.wireOp",EDGE,"E19.trimOffspring"),sQuery(id+"F0.wireOp",EDGE,"E20"),sQuery(id+"F0.wireOp",EDGE,"E21"),sQuery(id+"F0.wireOp",EDGE,"E22"),sQuery(id+"F0.wireOp",EDGE,"E23.top"),sQuery(id+"F0.wireOp",EDGE,"E23.left"),sQuery(id+"F0.wireOp",EDGE,"E23.right"),sQuery(id+"F0.wireOp",EDGE,"E24.trimOffspring")])],"isStart":true})],"blendedInto":[makeQuery(id+"F1.opExtrude","CAP_FACE",FACE,{"disambiguationData":[OSD([sQuery(id+"F0.wireOp",EDGE,"E1.top"),sQuery(id+"F0.wireOp",EDGE,"E2"),sQuery(id+"F0.wireOp",EDGE,"E3"),sQuery(id+"F0.wireOp",EDGE,"E4"),sQuery(id+"F0.wireOp",EDGE,"E5.top"),sQuery(id+"F0.wireOp",EDGE,"E5.left"),sQuery(id+"F0.wireOp",EDGE,"E5.right"),sQuery(id+"F0.wireOp",EDGE,"E6.trimOffspring"),subQ1,sQuery(id+"F0.wireOp",EDGE,"E7.right"),sQuery(id+"F0.wireOp",EDGE,"E8"),sQuery(id+"F0.wireOp",EDGE,"E9"),sQuery(id+"F0.wireOp",EDGE,"E10"),sQuery(id+"F0.wireOp",EDGE,"E11"),sQuery(id+"F0.wireOp",EDGE,"E12.1.0"),sQuery(id+"F0.wireOp",EDGE,"E12.1.1"),sQuery(id+"F0.wireOp",EDGE,"E12.3.0"),sQuery(id+"F0.wireOp",EDGE,"E12.3.1"),sQuery(id+"F0.wireOp",EDGE,"E12.4.0"),sQuery(id+"F0.wireOp",EDGE,"E12.4.1"),sQuery(id+"F0.wireOp",EDGE,"E13.trimOffspring"),subQ0,sQuery(id+"F0.wireOp",EDGE,"E15.trimOffspring"),sQuery(id+"F0.wireOp",EDGE,"E16.trimOffspring"),sQuery(id+"F0.wireOp",EDGE,"E17.trimOffspring"),sQuery(id+"F0.wireOp",EDGE,"E18.trimOffspring"),sQuery(id+"F0.wireOp",EDGE,"E19.trimOffspring"),sQuery(id+"F0.wireOp",EDGE,"E20"),sQuery(id+"F0.wireOp",EDGE,"E21"),sQuery(id+"F0.wireOp",EDGE,"E22"),sQuery(id+"F0.wireOp",EDGE,"E23.top"),sQuery(id+"F0.wireOp",EDGE,"E23.left"),sQuery(id+"F0.wireOp",EDGE,"E23.right"),sQuery(id+"F0.wireOp",EDGE,"E24.trimOffspring")])],"isStart":true})]});}
            var Q7;
            Q7=makeQuery(id+"F1.opExtrude","CAP_EDGE",EDGE,{"disambiguationData":[OSD([sQuery(id+"F0.wireOp",EDGE,"E14.trimOffspring")])],"isStart":true});
            var Q8;
            Q8=makeQuery(id+"F1.opExtrude","CAP_EDGE",EDGE,{"disambiguationData":[OSD([sQuery(id+"F0.wireOp",EDGE,"E12.3.1")])],"isStart":true});
            var Q9;
            Q9=makeQuery(id+"F1.opExtrude","CAP_EDGE",EDGE,{"disambiguationData":[OSD([sQuery(id+"F0.wireOp",EDGE,"E17.trimOffspring")])],"isStart":true});
            var Q10;
            Q10=makeQuery(id+"F1.opExtrude","CAP_EDGE",EDGE,{"disambiguationData":[OSD([sQuery(id+"F0.wireOp",EDGE,"E12.3.0")])],"isStart":true});
            var Q11;
            Q11=makeQuery(id+"F1.opExtrude","CAP_EDGE",EDGE,{"disambiguationData":[OSD([sQuery(id+"F0.wireOp",EDGE,"E12.4.1")])],"isStart":true});
            var Q12;
            Q12=makeQuery(id+"F1.opExtrude","CAP_EDGE",EDGE,{"disambiguationData":[OSD([sQuery(id+"F0.wireOp",EDGE,"E16.trimOffspring")])],"isStart":true});
            var Q13;
            Q13=makeQuery(id+"F1.opExtrude","CAP_EDGE",EDGE,{"disambiguationData":[OSD([sQuery(id+"F0.wireOp",EDGE,"E12.4.0"),sQuery(id+"F0.wireOp",EDGE,"E21")])],"isStart":true});
            var Q14;
            Q14=makeQuery(id+"F1.opExtrude","CAP_EDGE",EDGE,{"disambiguationData":[OSD([sQuery(id+"F0.wireOp",EDGE,"E10"),sQuery(id+"F0.wireOp",EDGE,"E22")])],"isStart":true});
            chamfer(context, id + "F18", {"entities" : qUnion([Q0, Q1, Q2, Q3, Q4, Q5, Q6, Q7, Q8, Q9, Q10, Q11, Q12, Q13, Q14]), "width" : 0.5 * mm, "tangentPropagation" : true});
        }
    });
